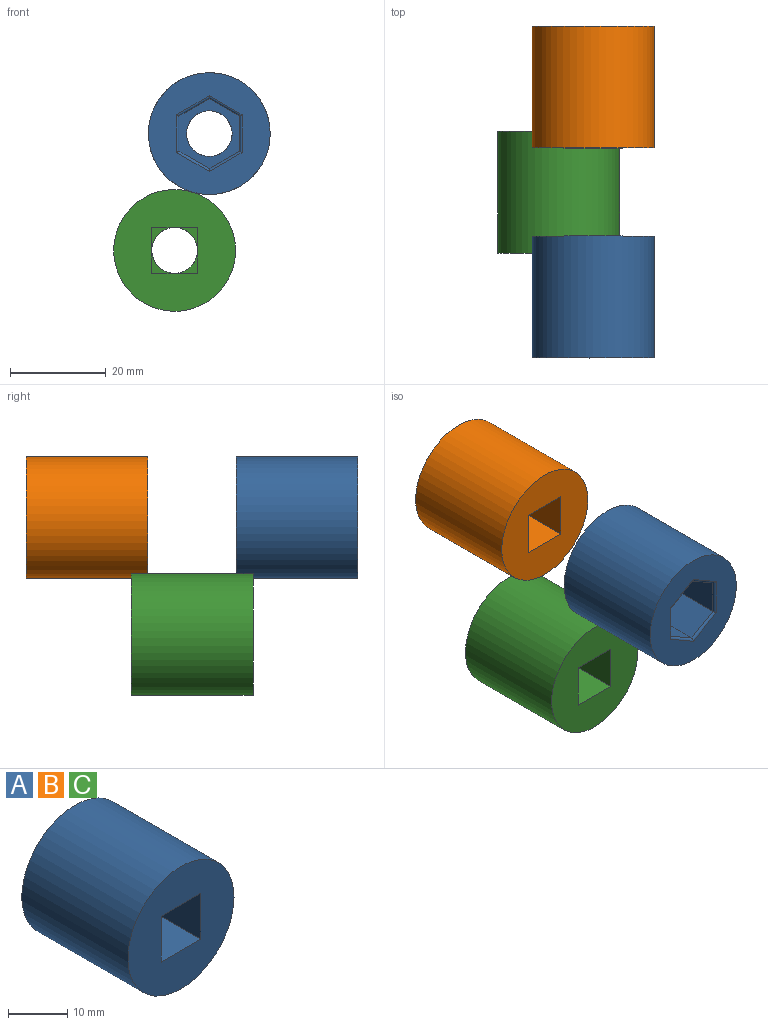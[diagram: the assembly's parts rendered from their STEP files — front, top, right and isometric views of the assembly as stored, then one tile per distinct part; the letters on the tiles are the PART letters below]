
ASSEMBLY  parts=3 mates=1
PART A: 25 faces, bbox 25.4x25.4x25.4 mm
  f0: cylinder r=4.76mm len=9.53mm, axis (0,-1,0), area 142.9mm2, adj f8,f9,f10,f11,f12
  f1: plane 25.4x25.4mm, normal (0,1,0), area 345mm2, adj f3,f19,f20,f21,f22,f23,f24
  f2: plane 25.4x25.4mm, normal (0,-1,0), area 416mm2, adj f3,f4,f5,f6,f7
  f3: cylinder r=12.7mm len=25.4mm, axis (0,1,0), area 2026.8mm2, adj f1,f2
  f4: plane 11.1x9.53mm, normal (-1,0,0), area 105.7mm2, adj f2,f5,f7,f10,f11
  f5: plane 11.1x9.53mm, normal (0,0,-1), area 105.7mm2, adj f2,f4,f6,f9,f10
  f6: plane 11.1x9.53mm, normal (1,0,0), area 105.7mm2, adj f2,f5,f7,f8,f9
  f7: plane 11.1x9.53mm, normal (0,0,1), area 105.7mm2, adj f2,f4,f6,f8,f11
  f8: plane 4.76x4.76mm, normal (0,-1,0), area 4.9mm2, adj f0,f6,f7
  f9: plane 4.76x4.76mm, normal (0,-1,0), area 4.9mm2, adj f0,f5,f6
  f10: plane 4.76x4.76mm, normal (0,-1,0), area 4.9mm2, adj f0,f4,f5
  f11: plane 4.76x4.76mm, normal (0,-1,0), area 4.9mm2, adj f0,f4,f7
  f12: plane 14.61x12.65mm, normal (0,1,0), area 67.3mm2, adj f0,f13,f14,f15,f16,f17,f18
  f13: plane 9.02x6.32mm, normal (-0.87,0,-0.5), area 65.8mm2, adj f12,f14,f18,f20
  f14: plane 9.02x6.32mm, normal (-0.87,0,0.5), area 65.8mm2, adj f12,f13,f15,f19
  f15: plane 9.02x7.3mm, normal (0,0,1), area 65.8mm2, adj f12,f14,f16,f21
  f16: plane 9.02x6.32mm, normal (0.87,0,0.5), area 65.8mm2, adj f12,f15,f17,f23
  f17: plane 9.02x6.32mm, normal (0.87,0,-0.5), area 65.8mm2, adj f12,f16,f18,f24
  f18: plane 9.02x7.3mm, normal (0,0,-1), area 65.8mm2, adj f12,f13,f17,f22
  f19: cylinder r=0.51mm len=7.09mm, axis (-0.5,0,-0.87), area 6mm2, adj f1,f14,f20,f21
  f20: cylinder r=0.51mm len=7.09mm, axis (0.5,0,-0.87), area 6mm2, adj f1,f13,f19,f22
  f21: cylinder r=0.51mm len=7.89mm, axis (-1,0,0), area 6mm2, adj f1,f15,f19,f23
  f22: cylinder r=0.51mm len=7.89mm, axis (1,0,0), area 6mm2, adj f1,f18,f20,f24
  f23: cylinder r=0.51mm len=7.09mm, axis (-0.5,0,0.87), area 6mm2, adj f1,f16,f21,f24
  f24: cylinder r=0.51mm len=7.09mm, axis (0.5,0,0.87), area 6mm2, adj f1,f17,f22,f23
PART B: same geometry as A
PART C: same geometry as A
PLACE A rot(axis=(-0.71,0,-0.71),180deg) t=(-14.47,-63.51,3.54)mm
PLACE B t=(-14.47,5.68,3.54)mm
PLACE C t=(-21.7,-16.25,-20.81)mm
MATE cylindrical A.f0 <-> B.f0  axis (0,1,0) through (-14.47,-38.11,3.54)mm
